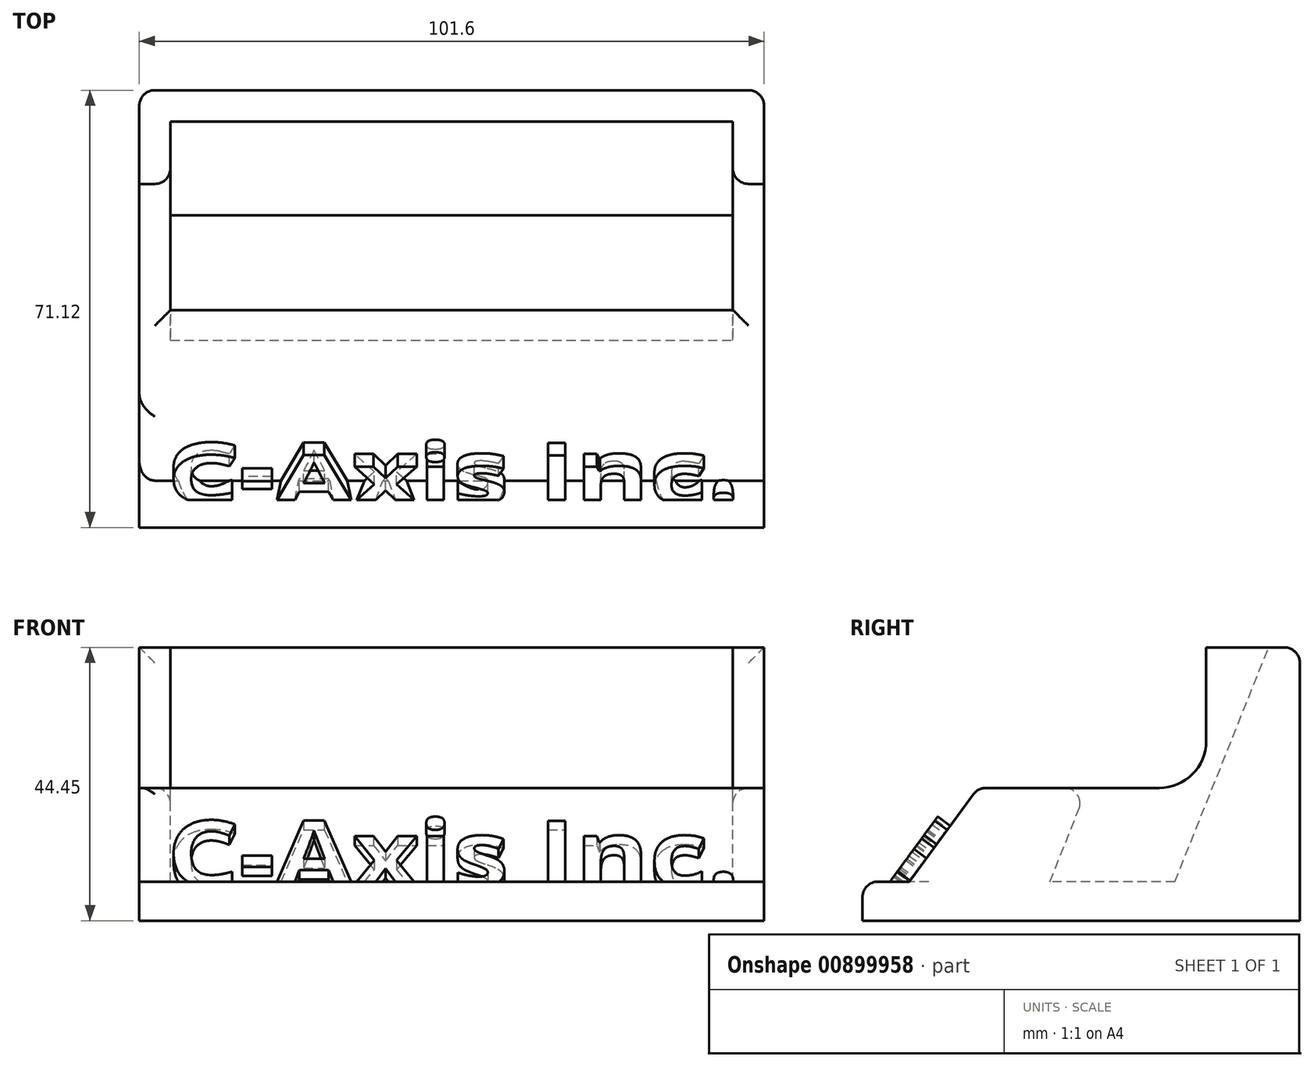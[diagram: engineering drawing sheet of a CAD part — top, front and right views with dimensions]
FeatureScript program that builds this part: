
annotation { "Feature Type Name" : "Feature", "Feature Type Description" : "" }
export const myFeature = defineFeature(function(context is Context, id is Id, definition is map)
    precondition{}
    {
        {
            var Q0;
            Q0=qCreatedBy(makeId("Top.planeOp"),FACE);
            var sketch = newSketch(context, id + "F0", { "sketchPlane" : qUnion([Q0])});
            skLineSegment(sketch, "E0.bottom", {"start": v(-50.8, 35.56) * mm, "end": v(50.8, 35.56) * mm});
            skLineSegment(sketch, "E0.top", {"start": v(-50.8, -35.56) * mm, "end": v(50.8, -35.56) * mm});
            skLineSegment(sketch, "E0.left", {"start": v(-50.8, 35.56) * mm, "end": v(-50.8, -35.56) * mm});
            skLineSegment(sketch, "E0.right", {"start": v(50.8, 35.56) * mm, "end": v(50.8, -35.56) * mm});
            skPoint(sketch, "E0.middle", {"position": v(0, 0) * mm});
            skSolve(sketch);
        }
        {
            var Q0;
            Q0=makeQuery(id+"F0.imprint","IMPRINT",FACE,{"disambiguationData":[TD([[makeQuery(id+"F0.imprint","IMPRINT",EDGE,{"derivedFrom":sQuery(id+"F0.wireOp",EDGE,"E0.bottom")}),-1.0]])]});
            extrude(context, id + "F1", {"entities" : qUnion([Q0]), "depth" : 6.35 * mm, "offsetDistance" : 25.4 * mm});
        }
        {
            var Q0;
            Q0=makeQuery(id+"F1.opExtrude","CAP_FACE",FACE,{"disambiguationData":[OSD([sQuery(id+"F0.wireOp",EDGE,"E0.bottom"),sQuery(id+"F0.wireOp",EDGE,"E0.top"),sQuery(id+"F0.wireOp",EDGE,"E0.left"),sQuery(id+"F0.wireOp",EDGE,"E0.right")])],"isStart":false});
            var sketch = newSketch(context, id + "F2", { "sketchPlane" : qUnion([Q0])});
            skLineSegment(sketch, "E1.bottom", {"start": v(-50.8, 35.56) * mm, "end": v(50.8, 35.56) * mm});
            skLineSegment(sketch, "E1.top", {"start": v(-50.8, -27.94) * mm, "end": v(50.8, -27.94) * mm});
            skLineSegment(sketch, "E1.left", {"start": v(-50.8, 35.56) * mm, "end": v(-50.8, -27.94) * mm});
            skLineSegment(sketch, "E1.right", {"start": v(50.8, 35.56) * mm, "end": v(50.8, -27.94) * mm});
            skSolve(sketch);
        }
        {
            var Q0;
            Q0=qSketchRegion(id+"F2",true);
            extrude(context, id + "F3", {"entities" : qUnion([Q0]), "operationType" : NewBodyOperationType.ADD, "depth" : 38.1 * mm, "offsetDistance" : 25.4 * mm});
        }
        {
            var Q0;
            Q0=makeQuery(id+"F3.boolean.opBoolean","MERGE",FACE,{"derivedFrom":[makeQuery(id+"F1.opExtrude","SWEPT_FACE",FACE,{"disambiguationData":[OSD([sQuery(id+"F0.wireOp",EDGE,"E0.right")])]}),makeQuery(id+"F3.opExtrude","SWEPT_FACE",FACE,{"disambiguationData":[OSD([sQuery(id+"F2.wireOp",EDGE,"E1.right")])]})]});
            var sketch = newSketch(context, id + "F4", { "sketchPlane" : qUnion([Q0])});
            skLineSegment(sketch, "E2", {"start": v(-27.94, 6.35) * mm, "end": v(0, 44.45) * mm});
            skLineSegment(sketch, "E3", {"start": v(0, 44.45) * mm, "end": v(-27.94, 44.45) * mm});
            skLineSegment(sketch, "E4", {"start": v(-27.94, 44.45) * mm, "end": v(-27.94, 6.35) * mm});
            skSolve(sketch);
        }
        {
            var Q0;
            Q0=qSketchRegion(id+"F4",true);
            extrude(context, id + "F5", {"entities" : qUnion([Q0]), "operationType" : NewBodyOperationType.REMOVE, "endBound" : BoundingType.THROUGH_ALL, "oppositeDirection" : true, "depth" : 25.4 * mm});
        }
        {
            var Q0;
            Q0=makeQuery(id+"F5.boolean.opBoolean","COPY",FACE,{"derivedFrom":makeQuery(id+"F5.opExtrude","SWEPT_FACE",FACE,{"disambiguationData":[OSD([sQuery(id+"F4.wireOp",EDGE,"E2")])]})});
            var sketch = newSketch(context, id + "F6", { "sketchPlane" : qUnion([Q0])});
            skText(sketch, "E5", { "text": "C-Axis Inc.", "fontName": "OpenSans-Bold.ttf"});
            const initialGuessF6  = {"E5": [-0.04628, -0.01408, 1, 0, 0.0132]};
            skSetInitialGuess(sketch, initialGuessF6);
            skSolve(sketch);
        }
        {
            var Q0;
            Q0=qSketchRegion(id+"F6",true);
            extrude(context, id + "F7", {"entities" : qUnion([Q0]), "operationType" : NewBodyOperationType.ADD, "depth" : 2.54 * mm, "offsetDistance" : 25.4 * mm});
        }
        {
            var Q0;
            Q0=qCreatedBy(makeId("Right.planeOp"),FACE);
            var sketch = newSketch(context, id + "F8", { "sketchPlane" : qUnion([Q0])});
            skLineSegment(sketch, "E6", {"start": v(15.24, 6.35) * mm, "end": v(30.48, 44.45) * mm});
            skLineSegment(sketch, "E7", {"start": v(-5.08, 6.35) * mm, "end": v(10.16, 44.45) * mm});
            skLineSegment(sketch, "E8", {"start": v(10.16, 44.45) * mm, "end": v(30.48, 44.45) * mm});
            skLineSegment(sketch, "E9", {"start": v(15.24, 6.35) * mm, "end": v(-5.08, 6.35) * mm});
            skSolve(sketch);
        }
        {
            var Q0;
            Q0=qSketchRegion(id+"F8",true);
            extrude(context, id + "F9", {"entities" : qUnion([Q0]), "operationType" : NewBodyOperationType.REMOVE, "oppositeDirection" : true, "depth" : 45.72 * mm, "hasSecondDirection" : true, "secondDirectionOppositeDirection" : false, "secondDirectionDepth" : 45.72 * mm});
        }
        {
            var Q0;
            Q0=qCreatedBy(makeId("Front.planeOp"),FACE);
            var sketch = newSketch(context, id + "F10", { "sketchPlane" : qUnion([Q0])});
            skLineSegment(sketch, "E10.bottom", {"start": v(50.8, 44.45) * mm, "end": v(-50.8, 44.45) * mm});
            skLineSegment(sketch, "E10.top", {"start": v(50.8, 21.59) * mm, "end": v(-50.8, 21.59) * mm});
            skLineSegment(sketch, "E10.left", {"start": v(50.8, 44.45) * mm, "end": v(50.8, 21.59) * mm});
            skLineSegment(sketch, "E10.right", {"start": v(-50.8, 44.45) * mm, "end": v(-50.8, 21.59) * mm});
            skSolve(sketch);
        }
        {
            var Q0;
            Q0=qSketchRegion(id+"F10",true);
            extrude(context, id + "F11", {"entities" : qUnion([Q0]), "operationType" : NewBodyOperationType.REMOVE, "oppositeDirection" : true, "depth" : 20.32 * mm, "hasSecondDirection" : true, "secondDirectionOppositeDirection" : false, "secondDirectionDepth" : 25.4 * mm, "offsetDistance" : 25.4 * mm});
        }
        {
            var Q0;
            Q0=makeQuery(id+"F11.boolean.opBoolean","COPY",EDGE,{"derivedFrom":makeQuery(id+"F11.opExtrude","CAP_EDGE",EDGE,{"disambiguationData":[OSD([sQuery(id+"F10.wireOp",EDGE,"E10.top")])],"isStart":false})});
            var Q1;
            Q1=makeQuery(id+"F11.boolean.opBoolean","COPY",EDGE,{"derivedFrom":makeQuery(id+"F11.opExtrude","CAP_EDGE",EDGE,{"disambiguationData":[OSD([sQuery(id+"F10.wireOp",EDGE,"E10.bottom")])],"isStart":false})});
            fillet(context, id + "F12", {"entities" : qUnion([Q0, Q1]), "radius" : 7.62 * mm, "tangentPropagation" : true, "allowEdgeOverflow" : false});
        }
        {
            var Q0;
            Q0=makeQuery(id+"F11.boolean.opBoolean","COPY",EDGE,{"derivedFrom":makeQuery(id+"F11.opExtrude","SWEPT_EDGE",EDGE,{"disambiguationData":[OSD([sQuery(id+"F10.wireOp",EDGE,"E10.top"),sQuery(id+"F10.wireOp",EDGE,"E10.left")])]})});
            var Q1;
            Q1=makeQuery(id+"F11.boolean.opBoolean","INTERSECT",EDGE,{"derivedFrom":[makeQuery(id+"F9.boolean.opBoolean","COPY",FACE,{"derivedFrom":makeQuery(id+"F9.opExtrude","CAP_FACE",FACE,{"disambiguationData":[OSD([sQuery(id+"F8.wireOp",EDGE,"E6"),sQuery(id+"F8.wireOp",EDGE,"E7"),sQuery(id+"F8.wireOp",EDGE,"E8"),sQuery(id+"F8.wireOp",EDGE,"E9")])],"isStart":true})}),makeQuery(id+"F11.opExtrude","SWEPT_FACE",FACE,{"disambiguationData":[OSD([sQuery(id+"F10.wireOp",EDGE,"E10.top")])]})]});
            var Q2;
            Q2=makeQuery(id+"F1.opExtrude","CAP_EDGE",EDGE,{"disambiguationData":[OSD([sQuery(id+"F0.wireOp",EDGE,"E0.top")])],"isStart":false});
            var Q3;
            Q3=makeQuery(id+"F5.boolean.opBoolean","INTERSECT",EDGE,{"derivedFrom":[makeQuery(id+"F3.boolean.opBoolean","MERGE",FACE,{"derivedFrom":[makeQuery(id+"F1.opExtrude","SWEPT_FACE",FACE,{"disambiguationData":[OSD([sQuery(id+"F0.wireOp",EDGE,"E0.left")])]}),makeQuery(id+"F3.opExtrude","SWEPT_FACE",FACE,{"disambiguationData":[OSD([sQuery(id+"F2.wireOp",EDGE,"E1.left")])]})]}),makeQuery(id+"F5.opExtrude","SWEPT_FACE",FACE,{"disambiguationData":[OSD([sQuery(id+"F4.wireOp",EDGE,"E2")])]})]});
            var Q4;
            Q4=makeQuery(id+"F5.boolean.opBoolean","COPY",EDGE,{"derivedFrom":makeQuery(id+"F5.opExtrude","CAP_EDGE",EDGE,{"disambiguationData":[OSD([sQuery(id+"F4.wireOp",EDGE,"E2")])],"isStart":true})});
            var Q5;
            Q5=makeQuery(id+"F11.boolean.opBoolean","COPY",EDGE,{"derivedFrom":makeQuery(id+"F11.opExtrude","SWEPT_EDGE",EDGE,{"disambiguationData":[OSD([sQuery(id+"F10.wireOp",EDGE,"E10.top"),sQuery(id+"F10.wireOp",EDGE,"E10.right")])]})});
            var Q6;
            Q6=makeQuery(id+"F11.boolean.opBoolean","INTERSECT",EDGE,{"derivedFrom":[makeQuery(id+"F9.boolean.opBoolean","COPY",FACE,{"derivedFrom":makeQuery(id+"F9.opExtrude","CAP_FACE",FACE,{"disambiguationData":[OSD([sQuery(id+"F8.wireOp",EDGE,"E6"),sQuery(id+"F8.wireOp",EDGE,"E7"),sQuery(id+"F8.wireOp",EDGE,"E8"),sQuery(id+"F8.wireOp",EDGE,"E9")])],"isStart":false})}),makeQuery(id+"F11.opExtrude","SWEPT_FACE",FACE,{"disambiguationData":[OSD([sQuery(id+"F10.wireOp",EDGE,"E10.top")])]})]});
            var Q7;
            Q7=makeQuery(id+"F3.boolean.opBoolean","MERGE",EDGE,{"derivedFrom":[makeQuery(id+"F1.opExtrude","SWEPT_EDGE",EDGE,{"disambiguationData":[OSD([sQuery(id+"F0.wireOp",EDGE,"E0.bottom"),sQuery(id+"F0.wireOp",EDGE,"E0.left")])]}),makeQuery(id+"F3.opExtrude","SWEPT_EDGE",EDGE,{"disambiguationData":[OSD([sQuery(id+"F2.wireOp",EDGE,"E1.bottom"),sQuery(id+"F2.wireOp",EDGE,"E1.left")])]})]});
            var Q8;
            Q8=makeQuery(id+"F3.boolean.opBoolean","MERGE",EDGE,{"derivedFrom":[makeQuery(id+"F1.opExtrude","SWEPT_EDGE",EDGE,{"disambiguationData":[OSD([sQuery(id+"F0.wireOp",EDGE,"E0.bottom"),sQuery(id+"F0.wireOp",EDGE,"E0.right")])]}),makeQuery(id+"F3.opExtrude","SWEPT_EDGE",EDGE,{"disambiguationData":[OSD([sQuery(id+"F2.wireOp",EDGE,"E1.bottom"),sQuery(id+"F2.wireOp",EDGE,"E1.right")])]})]});
            var Q9;
            Q9=makeQuery(id+"F3.opExtrude","CAP_EDGE",EDGE,{"disambiguationData":[OSD([sQuery(id+"F2.wireOp",EDGE,"E1.bottom")])],"isStart":false});
            var Q10;
            Q10=makeQuery(id+"F9.boolean.opBoolean","COPY",EDGE,{"derivedFrom":makeQuery(id+"F9.opExtrude","SWEPT_EDGE",EDGE,{"disambiguationData":[OSD([sQuery(id+"F8.wireOp",EDGE,"E6"),sQuery(id+"F8.wireOp",EDGE,"E8")])]})});
            var Q11;
            {var subQ1=sQuery(id+"F0.wireOp",EDGE,"E0.left");Q11=makeQuery(id+"F11.boolean.opBoolean","INTERSECT",EDGE,{"derivedFrom":[makeQuery(id+"F7.boolean.opBoolean","SPLIT",FACE,{"disambiguationData":[TD([makeQuery(id+"F1.opExtrude","SWEPT_FACE",FACE,{"disambiguationData":[OSD([subQ1])]})])],"derivedFrom":makeQuery(id+"F5.boolean.opBoolean","COPY",FACE,{"derivedFrom":makeQuery(id+"F5.opExtrude","SWEPT_FACE",FACE,{"disambiguationData":[OSD([sQuery(id+"F4.wireOp",EDGE,"E2")])]})})}),makeQuery(id+"F11.opExtrude","SWEPT_FACE",FACE,{"disambiguationData":[OSD([sQuery(id+"F10.wireOp",EDGE,"E10.top")])]})]});}
            var Q12;
            Q12=makeQuery(id+"F11.boolean.opBoolean","INTERSECT",EDGE,{"derivedFrom":[makeQuery(id+"F9.boolean.opBoolean","COPY",FACE,{"derivedFrom":makeQuery(id+"F9.opExtrude","SWEPT_FACE",FACE,{"disambiguationData":[OSD([sQuery(id+"F8.wireOp",EDGE,"E7")])]})}),makeQuery(id+"F11.opExtrude","SWEPT_FACE",FACE,{"disambiguationData":[OSD([sQuery(id+"F10.wireOp",EDGE,"E10.top")])]})]});
            fillet(context, id + "F13", {"entities" : qUnion([Q0, Q1, Q2, Q3, Q4, Q5, Q6, Q7, Q8, Q9, Q10, Q11, Q12]), "radius" : 2.54 * mm, "tangentPropagation" : true, "allowEdgeOverflow" : false});
        }
    });
